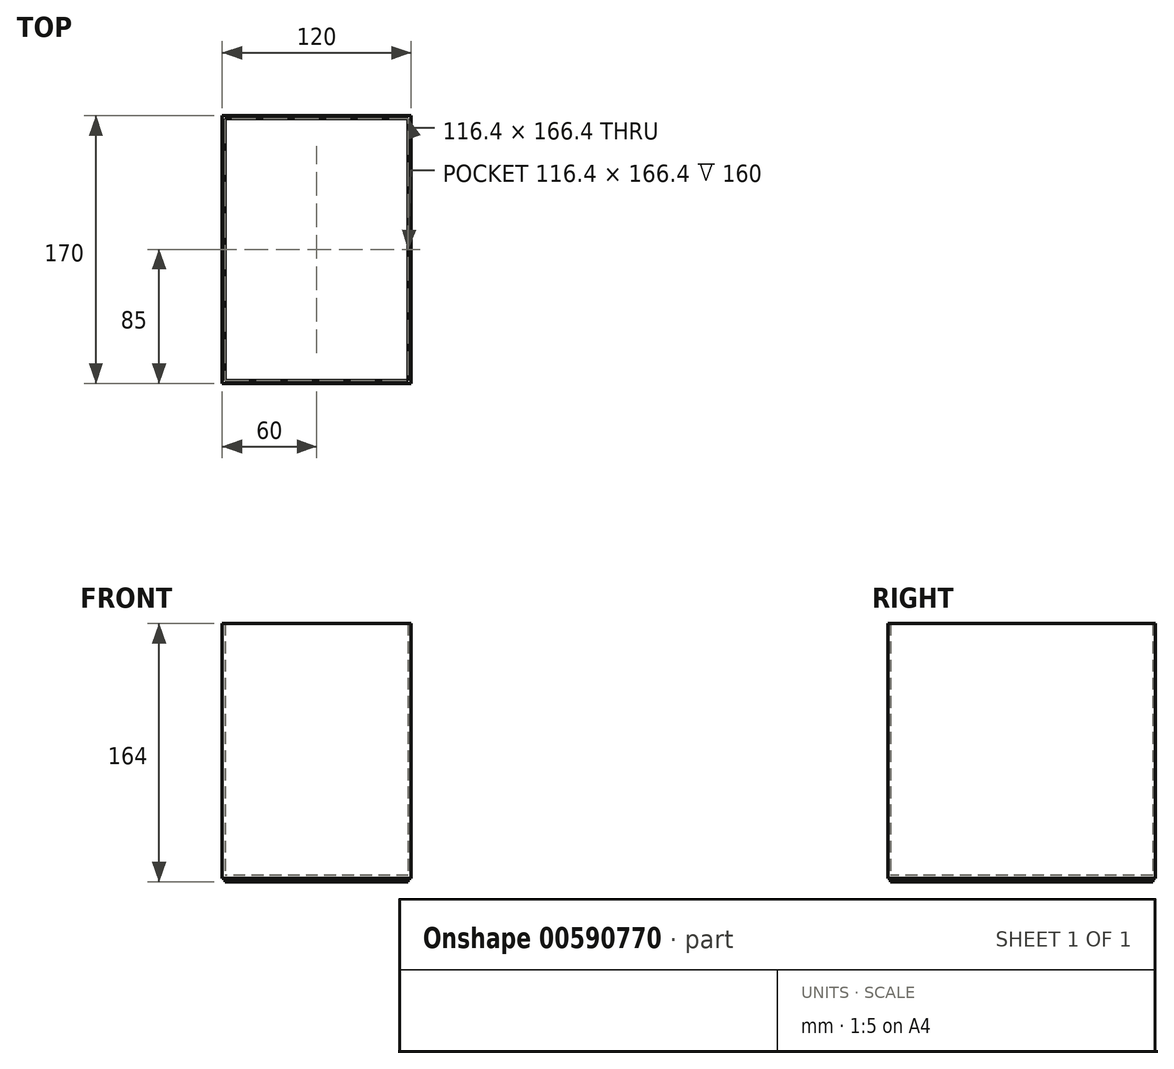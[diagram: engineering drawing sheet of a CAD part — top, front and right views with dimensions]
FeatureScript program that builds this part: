
annotation { "Feature Type Name" : "Feature", "Feature Type Description" : "" }
export const myFeature = defineFeature(function(context is Context, id is Id, definition is map)
    precondition{}
    {
        {
            var Q0;
            Q0=qCreatedBy(makeId("Top.planeOp"),FACE);
            var sketch = newSketch(context, id + "F0", { "sketchPlane" : qUnion([Q0])});
            skLineSegment(sketch, "E0.bottom", {"start": v(60, 85) * mm, "end": v(-60, 85) * mm});
            skLineSegment(sketch, "E0.top", {"start": v(60, -85) * mm, "end": v(-60, -85) * mm});
            skLineSegment(sketch, "E0.left", {"start": v(60, 85) * mm, "end": v(60, -85) * mm});
            skLineSegment(sketch, "E0.right", {"start": v(-60, 85) * mm, "end": v(-60, -85) * mm});
            skPoint(sketch, "E0.middle", {"position": v(0, 0) * mm});
            skLineSegment(sketch, "E1.0", {"start": v(58.2, 83.2) * mm, "end": v(-58.2, 83.2) * mm});
            skLineSegment(sketch, "E1.1", {"start": v(58.2, 83.2) * mm, "end": v(58.2, -83.2) * mm});
            skLineSegment(sketch, "E1.2", {"start": v(58.2, -83.2) * mm, "end": v(-58.2, -83.2) * mm});
            skLineSegment(sketch, "E1.3", {"start": v(-58.2, 83.2) * mm, "end": v(-58.2, -83.2) * mm});
            skSolve(sketch);
        }
        {
            var Q0;
            Q0=makeQuery(id+"F0.imprint","IMPRINT",FACE,{"disambiguationData":[TD([[makeQuery(id+"F0.imprint","IMPRINT",EDGE,{"derivedFrom":sQuery(id+"F0.wireOp",EDGE,"E0.bottom")}),1.0]])]});
            extrude(context, id + "F1", {"entities" : qUnion([Q0]), "depth" : (170 - 8) * mm, "offsetDistance" : 25 * mm});
        }
        {
            var Q0;
            Q0=makeQuery(id+"F0.imprint","IMPRINT",FACE,{"disambiguationData":[TD([[makeQuery(id+"F0.imprint","IMPRINT",EDGE,{"derivedFrom":sQuery(id+"F0.wireOp",EDGE,"E1.0")}),1.0]])]});
            extrude(context, id + "F2", {"entities" : qUnion([Q0]), "operationType" : NewBodyOperationType.ADD, "endBound" : BoundingType.SYMMETRIC, "depth" : 4 * mm, "offsetDistance" : 25 * mm});
        }
    });
